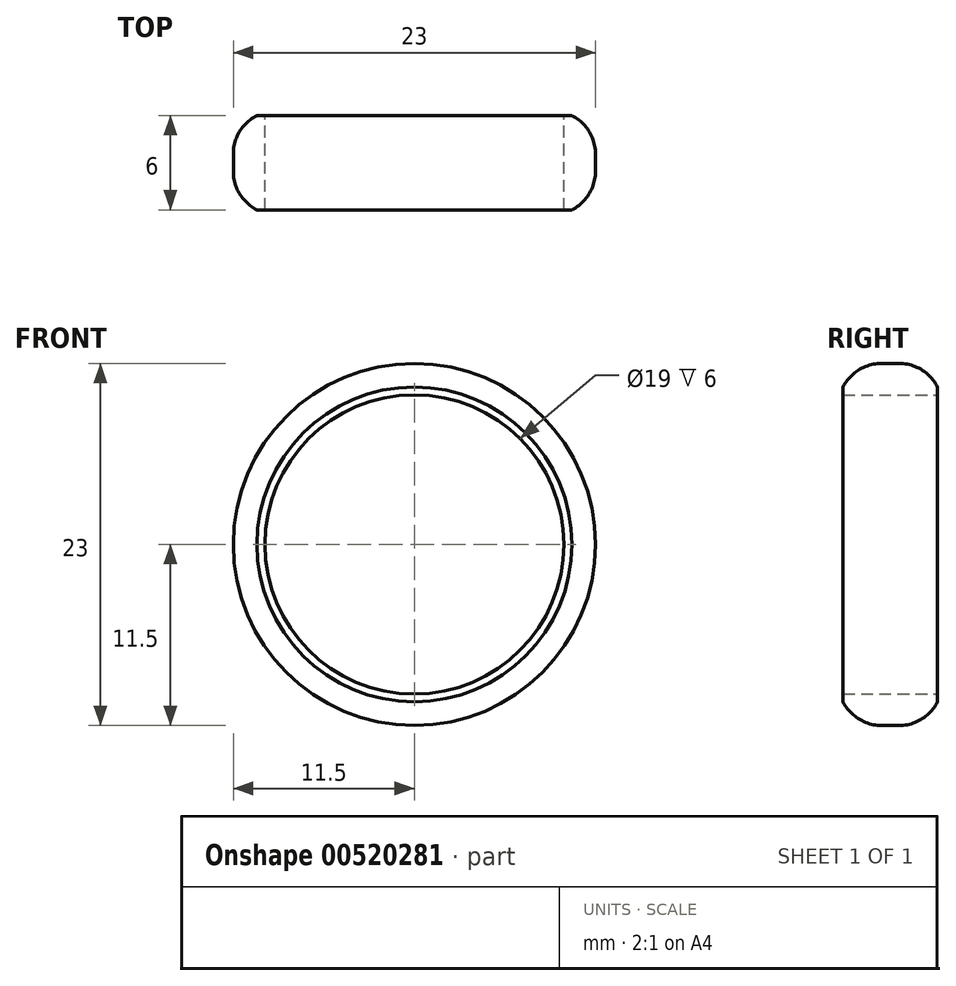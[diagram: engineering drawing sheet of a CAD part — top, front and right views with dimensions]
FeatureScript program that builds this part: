
annotation { "Feature Type Name" : "Feature", "Feature Type Description" : "" }
export const myFeature = defineFeature(function(context is Context, id is Id, definition is map)
    precondition{}
    {
        {
            var Q0;
            Q0=qCreatedBy(makeId("Front.planeOp"),FACE);
            var sketch = newSketch(context, id + "F0", { "sketchPlane" : qUnion([Q0])});
            skCircle(sketch, "E0", {"center": v(0, 0) * mm, "radius": 9.5 * mm});
            skCircle(sketch, "E1", {"center": v(0, 0) * mm, "radius": 11.5 * mm});
            skCircle(sketch, "E2", {"center": v(0, 0) * mm, "radius": 10 * mm});
            skSolve(sketch);
        }
        {
            var Q0;
            Q0=makeQuery(id+"F0.imprint","IMPRINT",FACE,{"disambiguationData":[TD([[makeQuery(id+"F0.imprint","IMPRINT",EDGE,{"derivedFrom":sQuery(id+"F0.wireOp",EDGE,"E1")}),1.0]])]});
            extrude(context, id + "F1", {"entities" : qUnion([Q0]), "depth" : 6 * mm, "offsetDistance" : 25 * mm});
        }
        {
            var Q0;
            Q0=makeQuery(id+"F1.opExtrude","SWEPT_FACE",FACE,{"disambiguationData":[OSD([sQuery(id+"F0.wireOp",EDGE,"E1")])]});
            var Q1;
            Q1=makeQuery(id+"F1.opExtrude","CAP_EDGE",EDGE,{"disambiguationData":[OSD([sQuery(id+"F0.wireOp",EDGE,"E1")])],"isStart":true});
            fillet(context, id + "F2", {"entities" : qUnion([Q0, Q1]), "radius" : 2.75 * mm, "tangentPropagation" : true, "defaultsChanged" : true, "vertexSettings" : [], "allowEdgeOverflow" : false});
        }
        {
            var Q0;
            Q0=makeQuery(id+"F0.imprint","IMPRINT",FACE,{"disambiguationData":[TD([[makeQuery(id+"F0.imprint","IMPRINT",EDGE,{"derivedFrom":sQuery(id+"F0.wireOp",EDGE,"E0")}),-1.0]])]});
            extrude(context, id + "F3", {"entities" : qUnion([Q0]), "operationType" : NewBodyOperationType.ADD, "depth" : 6 * mm, "offsetDistance" : 25 * mm});
        }
    });
